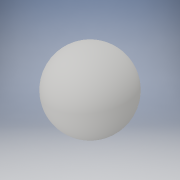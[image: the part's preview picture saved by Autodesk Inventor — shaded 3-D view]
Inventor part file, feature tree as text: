
AUTODESK INVENTOR PART (.ipt)
format: ipt  version: 2019 (Build 230136000, 136)  size: 118,784 bytes
history: native  units: in
note: dims shown in document units (in); Inventor stores cm internally (conversion verified against a paired STEP export)
features: revolve x1, sketch x1
ambient origin geometry x8: Origin, YZ Plane, XZ Plane, XY Plane, X Axis, Y Axis, Z Axis, Center Point
bodies: Solid1 (feature_tree)
feature tree (2):
  revolve  "Revolution1"  [1 undecoded]
  sketch  "Sketch1"  dims[d0=0.875in d1=0.4375in d2=0.4375in d3=90.0deg]
note: 1 required parameter value undecoded (feature->parameter linkage not recoverable at this tier; creation-order binding heuristic only, values carry confidence <= 0.55)
